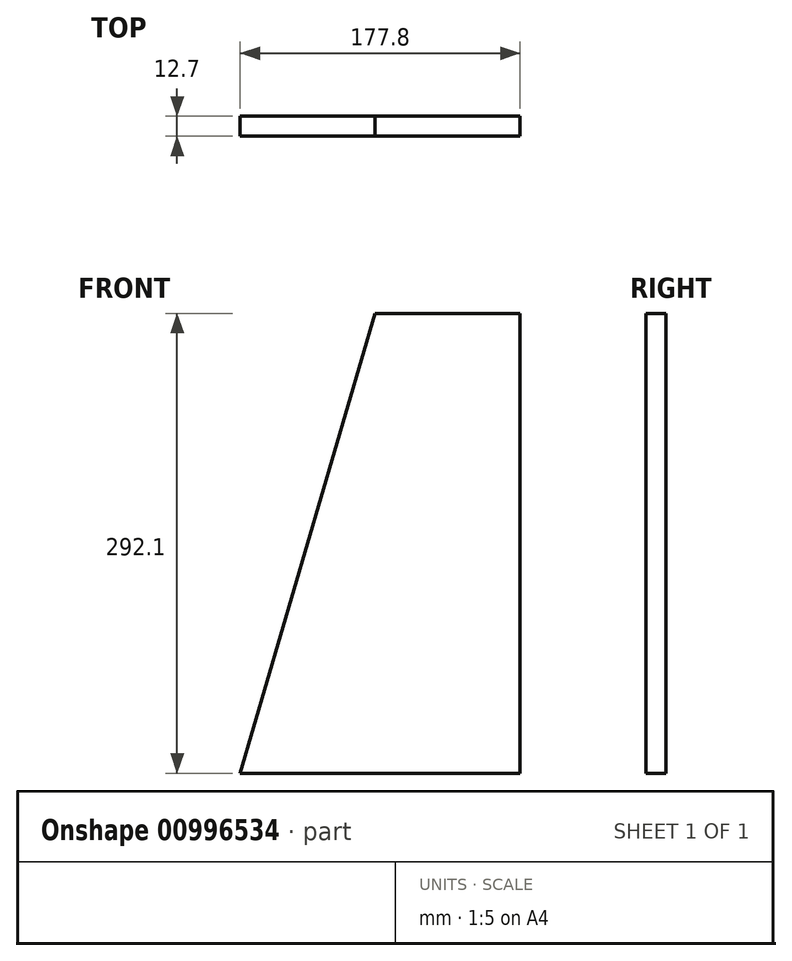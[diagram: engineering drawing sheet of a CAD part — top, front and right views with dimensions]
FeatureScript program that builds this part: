
annotation { "Feature Type Name" : "Feature", "Feature Type Description" : "" }
export const myFeature = defineFeature(function(context is Context, id is Id, definition is map)
    precondition{}
    {
        {
            var Q0;
            Q0=qCreatedBy(makeId("Front.planeOp"),FACE);
            var sketch = newSketch(context, id + "F0", { "sketchPlane" : qUnion([Q0])});
            skLineSegment(sketch, "E0.bottom", {"start": v(88.9, 146.05) * mm, "end": v(-88.9, 146.05) * mm});
            skLineSegment(sketch, "E0.top", {"start": v(88.9, -146.05) * mm, "end": v(-88.9, -146.05) * mm});
            skLineSegment(sketch, "E0.left", {"start": v(88.9, 146.05) * mm, "end": v(88.9, -146.05) * mm});
            skLineSegment(sketch, "E0.right", {"start": v(-88.9, 146.05) * mm, "end": v(-88.9, -146.05) * mm});
            skPoint(sketch, "E0.middle", {"position": v(0, 0) * mm});
            skSolve(sketch);
        }
        {
            var Q0;
            Q0=makeQuery(id+"F0.imprint","IMPRINT",FACE,{"disambiguationData":[TD([[makeQuery(id+"F0.imprint","IMPRINT",EDGE,{"derivedFrom":sQuery(id+"F0.wireOp",EDGE,"E0.bottom")}),1.0]])]});
            extrude(context, id + "F1", {"entities" : qUnion([Q0]), "depth" : 12.7 * mm, "offsetDistance" : 25.4 * mm});
        }
        {
            var Q0;
            Q0=makeQuery(id+"F1.opExtrude","SWEPT_EDGE",EDGE,{"disambiguationData":[OSD([sQuery(id+"F0.wireOp",EDGE,"E0.bottom"),sQuery(id+"F0.wireOp",EDGE,"E0.right")])]});
            chamfer(context, id + "F2", {"entities" : qUnion([Q0]), "chamferType" : ChamferType.TWO_OFFSETS, "width1" : 292.1 * mm, "oppositeDirection" : false, "width2" : 85.72 * mm, "tangentPropagation" : true});
        }
    });
